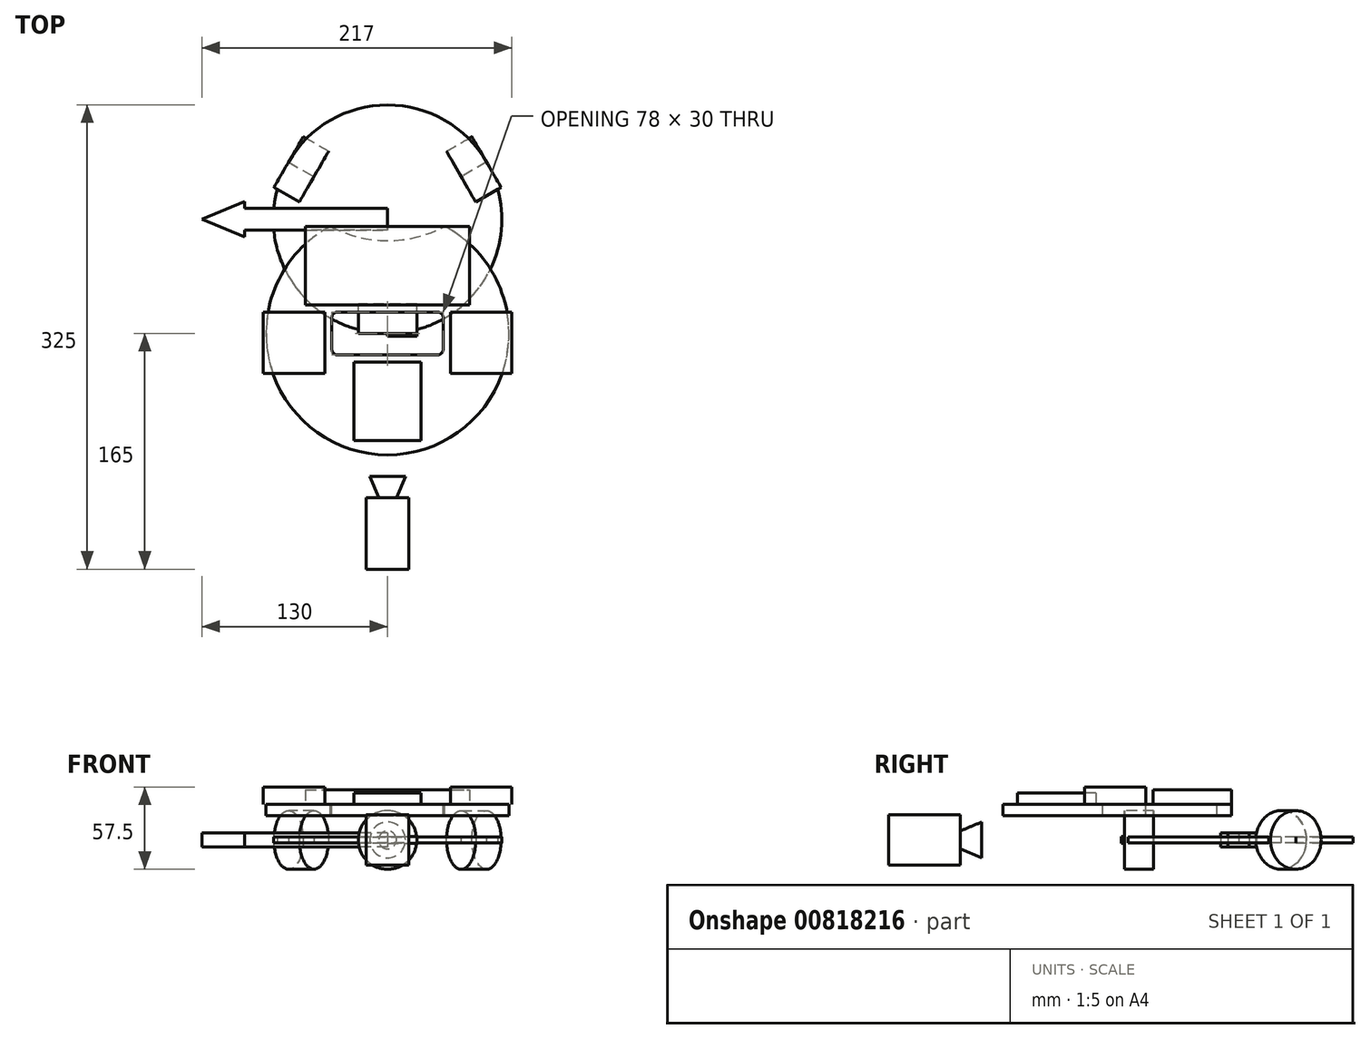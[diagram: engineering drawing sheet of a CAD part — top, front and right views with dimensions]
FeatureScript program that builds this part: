
annotation { "Feature Type Name" : "Feature", "Feature Type Description" : "" }
export const myFeature = defineFeature(function(context is Context, id is Id, definition is map)
    precondition{}
    {
        {
            var Q0;
            Q0=qCreatedBy(makeId("Top.planeOp"),FACE);
            var sketch = newSketch(context, id + "F0", { "sketchPlane" : qUnion([Q0])});
            skLineSegment(sketch, "E0.bottom", {"start": v(0, 0) * mm, "end": v(20.5, 0) * mm});
            skLineSegment(sketch, "E0.top", {"start": v(0, 20.5) * mm, "end": v(20.5, 20.5) * mm});
            skLineSegment(sketch, "E0.left", {"start": v(0, 0) * mm, "end": v(0, 20.5) * mm});
            skLineSegment(sketch, "E0.right", {"start": v(20.5, 0) * mm, "end": v(20.5, 20.5) * mm});
            skLineSegment(sketch, "E1", {"start": v(0, -100) * mm, "end": v(12.5, -100) * mm});
            skLineSegment(sketch, "E2", {"start": v(12.5, -100) * mm, "end": v(0, -130) * mm});
            skLineSegment(sketch, "E3.bottom", {"start": v(15, -115) * mm, "end": v(-15, -115) * mm});
            skLineSegment(sketch, "E3.top", {"start": v(15, -165) * mm, "end": v(-15, -165) * mm});
            skLineSegment(sketch, "E3.left", {"start": v(15, -115) * mm, "end": v(15, -165) * mm});
            skLineSegment(sketch, "E3.right", {"start": v(-15, -115) * mm, "end": v(-15, -165) * mm});
            skLineSegment(sketch, "E4", {"start": v(0, -100) * mm, "end": v(0, -130) * mm});
            skLineSegment(sketch, "E5.top", {"start": v(0, -2) * mm, "end": v(20.5, -2) * mm});
            skLineSegment(sketch, "E5.left", {"start": v(0, 0) * mm, "end": v(0, -2) * mm});
            skLineSegment(sketch, "E5.right", {"start": v(20.5, 0) * mm, "end": v(20.5, -2) * mm});
            skCircle(sketch, "E6", {"center": v(0, 80) * mm, "radius": 80 * mm});
            skLineSegment(sketch, "E7.bottom", {"start": v(0, 0) * mm, "end": v(-20.5, 0) * mm});
            skLineSegment(sketch, "E7.top", {"start": v(0, 20.5) * mm, "end": v(-20.5, 20.5) * mm});
            skLineSegment(sketch, "E7.right", {"start": v(-20.5, 0) * mm, "end": v(-20.5, 20.5) * mm});
            skLineSegment(sketch, "E8", {"start": v(-69.28, 40) * mm, "end": v(0, 80) * mm});
            skLineSegment(sketch, "E9", {"start": v(0, 80) * mm, "end": v(69.28, 40) * mm});
            skLineSegment(sketch, "E10", {"start": v(0, 0) * mm, "end": v(0, 80) * mm});
            skLineSegment(sketch, "E11.MirrorCS", {"start": v(79.53, 102.25) * mm, "end": v(61.78, 92) * mm});
            skLineSegment(sketch, "E12.MirrorCS", {"start": v(51.53, 109.75) * mm, "end": v(61.78, 92) * mm});
            skLineSegment(sketch, "E13.MirrorCS", {"start": v(69.28, 120) * mm, "end": v(51.53, 109.75) * mm});
            skLineSegment(sketch, "E14.MirrorCS", {"start": v(69.28, 120) * mm, "end": v(79.53, 102.25) * mm});
            skLineSegment(sketch, "E15.MirrorCS", {"start": v(-51.53, 109.75) * mm, "end": v(-61.78, 92) * mm});
            skLineSegment(sketch, "E16.MirrorCS", {"start": v(-79.53, 102.25) * mm, "end": v(-61.78, 92) * mm});
            skLineSegment(sketch, "E17.MirrorCS", {"start": v(-69.28, 120) * mm, "end": v(-79.53, 102.25) * mm});
            skLineSegment(sketch, "E18.MirrorCS", {"start": v(-69.28, 120) * mm, "end": v(-51.53, 109.75) * mm});
            skLineSegment(sketch, "E19.bottom", {"start": v(0, 72.5) * mm, "end": v(-100, 72.5) * mm});
            skLineSegment(sketch, "E19.top", {"start": v(0, 87.5) * mm, "end": v(-100, 87.5) * mm});
            skLineSegment(sketch, "E19.left", {"start": v(0, 72.5) * mm, "end": v(0, 87.5) * mm});
            skLineSegment(sketch, "E19.right", {"start": v(-100, 72.5) * mm, "end": v(-100, 87.5) * mm});
            skLineSegment(sketch, "E20", {"start": v(-130, 80) * mm, "end": v(-100, 67.5) * mm});
            skLineSegment(sketch, "E21", {"start": v(-130, 80) * mm, "end": v(0, 80) * mm});
            skLineSegment(sketch, "E22", {"start": v(-100, 72.5) * mm, "end": v(-100, 67.5) * mm});
            skLineSegment(sketch, "E23.MirrorCS", {"start": v(-130, 80) * mm, "end": v(-100, 92.5) * mm});
            skLineSegment(sketch, "E24.MirrorCS", {"start": v(-100, 87.5) * mm, "end": v(-100, 92.5) * mm});
            skSolve(sketch);
        }
        {
            var Q0;
            {var subQ0=sQuery(id+"F0.wireOp",EDGE,"E0.top");Q0=makeQuery(id+"F0.imprint","IMPRINT",FACE,{"disambiguationData":[TD([[makeQuery(id+"F0.imprint","IMPRINT",EDGE,{"derivedFrom":subQ0}),1.0]])]});}
            var Q1;
            {var subQ2=sQuery(id+"F0.wireOp",EDGE,"E7.top");Q1=makeQuery(id+"F0.imprint","IMPRINT",FACE,{"disambiguationData":[TD([[makeQuery(id+"F0.imprint","IMPRINT",EDGE,{"derivedFrom":subQ2}),-1.0]])]});}
            var Q2;
            {var subQ0=sQuery(id+"F0.wireOp",EDGE,"E8");Q2=makeQuery(id+"F0.imprint","IMPRINT",FACE,{"disambiguationData":[TD([[makeQuery(id+"F0.imprint","IMPRINT",EDGE,{"derivedFrom":subQ0}),1.0]])]});}
            var Q3;
            {var subQ11=sQuery(id+"F0.wireOp",EDGE,"E9");Q3=makeQuery(id+"F0.imprint","IMPRINT",FACE,{"disambiguationData":[TD([[makeQuery(id+"F0.imprint","IMPRINT",EDGE,{"derivedFrom":subQ11}),1.0]])]});}
            var Q4;
            {var subQ0=sQuery(id+"F0.wireOp",EDGE,"E19.bottom");var subQ1=sQuery(id+"F0.wireOp",EDGE,"E6");var subQ2=makeQuery(id+"F0.imprint","INTERSECT",VERTEX,{"derivedFrom":[subQ1,subQ0]});Q4=makeQuery(id+"F0.imprint","IMPRINT",FACE,{"disambiguationData":[TD([[makeQuery(id+"F0.imprint","IMPRINT",EDGE,{"disambiguationData":[TD([[subQ2,1.0]])],"derivedFrom":subQ1}),1.0]])]});}
            var Q5;
            {var subQ0=sQuery(id+"F0.wireOp",EDGE,"E19.top");var subQ1=sQuery(id+"F0.wireOp",EDGE,"E6");var subQ2=makeQuery(id+"F0.imprint","INTERSECT",VERTEX,{"derivedFrom":[subQ1,subQ0]});Q5=makeQuery(id+"F0.imprint","IMPRINT",FACE,{"disambiguationData":[TD([[makeQuery(id+"F0.imprint","IMPRINT",EDGE,{"disambiguationData":[TD([[subQ2,-1.0]])],"derivedFrom":subQ1}),1.0]])]});}
            var Q6;
            {var subQ1=sQuery(id+"F0.wireOp",EDGE,"E8");var subQ3=sQuery(id+"F0.wireOp",EDGE,"E19.bottom");var subQ4=makeQuery(id+"F0.imprint","INTERSECT",VERTEX,{"derivedFrom":[subQ1,subQ3]});Q6=makeQuery(id+"F0.imprint","IMPRINT",FACE,{"disambiguationData":[TD([[makeQuery(id+"F0.imprint","IMPRINT",EDGE,{"disambiguationData":[TD([[subQ4,1.0]])],"derivedFrom":subQ3}),-1.0]])]});}
            extrude(context, id + "F1", {"entities" : qUnion([Q0, Q1, Q2, Q3, Q4, Q5, Q6]), "endBound" : BoundingType.SYMMETRIC, "depth" : 4 * mm, "offsetDistance" : 25 * mm});
        }
        {
            var Q0;
            {var subQ0=sQuery(id+"F0.wireOp",EDGE,"E0.top");Q0=makeQuery(id+"F0.imprint","IMPRINT",FACE,{"disambiguationData":[TD([[makeQuery(id+"F0.imprint","IMPRINT",EDGE,{"derivedFrom":subQ0}),-1.0]])]});}
            var Q1;
            {var subQ0=sQuery(id+"F0.wireOp",EDGE,"E0.bottom");Q1=makeQuery(id+"F0.imprint","IMPRINT",FACE,{"disambiguationData":[TD([[makeQuery(id+"F0.imprint","IMPRINT",EDGE,{"derivedFrom":subQ0}),1.0]])]});}
            var Q2;
            Q2=sQuery(id+"F0.wireOp",EDGE,"E0.left");
            revolve(context, id + "F2", {"surfaceOperationType" : NewSurfaceOperationType.NEW, "entities" : qUnion([Q0, Q1]), "axis" : qUnion([Q2]), "revolveType" : RevolveType.FULL});
        }
        {
            var Q0;
            {var subQ0=sQuery(id+"F0.wireOp",EDGE,"E1");Q0=makeQuery(id+"F0.imprint","IMPRINT",FACE,{"disambiguationData":[TD([[makeQuery(id+"F0.imprint","IMPRINT",EDGE,{"derivedFrom":subQ0}),-1.0]])]});}
            var Q1;
            Q1=sQuery(id+"F0.wireOp",EDGE,"E4");
            revolve(context, id + "F3", {"surfaceOperationType" : NewSurfaceOperationType.NEW, "entities" : qUnion([Q0]), "axis" : qUnion([Q1]), "revolveType" : RevolveType.FULL});
        }
        {
            var Q0;
            Q0=makeQuery(id+"F0.imprint","IMPRINT",FACE,{"disambiguationData":[TD([[makeQuery(id+"F0.imprint","IMPRINT",EDGE,{"derivedFrom":sQuery(id+"F0.wireOp",EDGE,"E3.top")}),-1.0]])]});
            var Q1;
            {var subQ0=sQuery(id+"F0.wireOp",EDGE,"E4");var subQ1=sQuery(id+"F0.wireOp",EDGE,"E2");var subQ2=makeQuery(id+"F0.imprint","INTERSECT",VERTEX,{"derivedFrom":[subQ1,subQ0]});Q1=makeQuery(id+"F0.imprint","IMPRINT",FACE,{"disambiguationData":[TD([[makeQuery(id+"F0.imprint","IMPRINT",EDGE,{"disambiguationData":[TD([[subQ2,1.0]])],"derivedFrom":subQ1}),-1.0]])]});}
            extrude(context, id + "F4", {"entities" : qUnion([Q0, Q1]), "operationType" : NewBodyOperationType.ADD, "endBound" : BoundingType.SYMMETRIC, "depth" : 35 * mm, "offsetDistance" : 25 * mm});
        }
        {
            var Q0;
            Q0=makeQuery(id+"F0.imprint","IMPRINT",FACE,{"disambiguationData":[TD([[makeQuery(id+"F0.imprint","IMPRINT",EDGE,{"derivedFrom":sQuery(id+"F0.wireOp",EDGE,"E0.bottom")}),-1.0]])]});
            extrude(context, id + "F5", {"entities" : qUnion([Q0]), "endBound" : BoundingType.SYMMETRIC, "depth" : 5 * mm, "offsetDistance" : 25 * mm});
        }
        {
            var Q0;
            {var subQ4=sQuery(id+"F0.wireOp",EDGE,"E12.MirrorCS");Q0=makeQuery(id+"F0.imprint","IMPRINT",FACE,{"disambiguationData":[TD([[makeQuery(id+"F0.imprint","IMPRINT",EDGE,{"derivedFrom":subQ4}),1.0]])]});}
            var Q1;
            {var subQ0=sQuery(id+"F0.wireOp",EDGE,"E14.MirrorCS");Q1=makeQuery(id+"F0.imprint","IMPRINT",FACE,{"disambiguationData":[TD([[makeQuery(id+"F0.imprint","IMPRINT",EDGE,{"derivedFrom":subQ0}),-1.0]])]});}
            var Q2;
            Q2=sQuery(id+"F0.wireOp",EDGE,"E13.MirrorCS");
            revolve(context, id + "F6", {"surfaceOperationType" : NewSurfaceOperationType.NEW, "entities" : qUnion([Q0, Q1]), "axis" : qUnion([Q2]), "revolveType" : RevolveType.FULL});
        }
        {
            var Q0;
            {var subQ4=sQuery(id+"F0.wireOp",EDGE,"E15.MirrorCS");Q0=makeQuery(id+"F0.imprint","IMPRINT",FACE,{"disambiguationData":[TD([[makeQuery(id+"F0.imprint","IMPRINT",EDGE,{"derivedFrom":subQ4}),-1.0]])]});}
            var Q1;
            {var subQ0=sQuery(id+"F0.wireOp",EDGE,"E17.MirrorCS");Q1=makeQuery(id+"F0.imprint","IMPRINT",FACE,{"disambiguationData":[TD([[makeQuery(id+"F0.imprint","IMPRINT",EDGE,{"derivedFrom":subQ0}),1.0]])]});}
            var Q2;
            Q2=sQuery(id+"F0.wireOp",EDGE,"E18.MirrorCS");
            revolve(context, id + "F7", {"surfaceOperationType" : NewSurfaceOperationType.NEW, "entities" : qUnion([Q0, Q1]), "axis" : qUnion([Q2]), "revolveType" : RevolveType.FULL});
        }
        {
            var Q0;
            {var subQ4=sQuery(id+"F0.wireOp",EDGE,"E20");Q0=makeQuery(id+"F0.imprint","IMPRINT",FACE,{"disambiguationData":[TD([[makeQuery(id+"F0.imprint","IMPRINT",EDGE,{"derivedFrom":subQ4}),1.0]])]});}
            var Q1;
            {var subQ4=sQuery(id+"F0.wireOp",EDGE,"E23.MirrorCS");Q1=makeQuery(id+"F0.imprint","IMPRINT",FACE,{"disambiguationData":[TD([[makeQuery(id+"F0.imprint","IMPRINT",EDGE,{"derivedFrom":subQ4}),-1.0]])]});}
            var Q2;
            {var subQ0=sQuery(id+"F0.wireOp",EDGE,"E19.top");var subQ1=sQuery(id+"F0.wireOp",EDGE,"E6");var subQ2=makeQuery(id+"F0.imprint","INTERSECT",VERTEX,{"derivedFrom":[subQ1,subQ0]});Q2=makeQuery(id+"F0.imprint","IMPRINT",FACE,{"disambiguationData":[TD([[makeQuery(id+"F0.imprint","IMPRINT",EDGE,{"disambiguationData":[TD([[subQ2,-1.0]])],"derivedFrom":subQ1}),-1.0]])]});}
            var Q3;
            {var subQ0=sQuery(id+"F0.wireOp",EDGE,"E19.bottom");var subQ1=sQuery(id+"F0.wireOp",EDGE,"E6");var subQ2=makeQuery(id+"F0.imprint","INTERSECT",VERTEX,{"derivedFrom":[subQ1,subQ0]});Q3=makeQuery(id+"F0.imprint","IMPRINT",FACE,{"disambiguationData":[TD([[makeQuery(id+"F0.imprint","IMPRINT",EDGE,{"disambiguationData":[TD([[subQ2,1.0]])],"derivedFrom":subQ1}),-1.0]])]});}
            var Q4;
            {var subQ0=sQuery(id+"F0.wireOp",EDGE,"E19.top");var subQ1=sQuery(id+"F0.wireOp",EDGE,"E6");var subQ2=makeQuery(id+"F0.imprint","INTERSECT",VERTEX,{"derivedFrom":[subQ1,subQ0]});Q4=makeQuery(id+"F0.imprint","IMPRINT",FACE,{"disambiguationData":[TD([[makeQuery(id+"F0.imprint","IMPRINT",EDGE,{"disambiguationData":[TD([[subQ2,-1.0]])],"derivedFrom":subQ1}),1.0]])]});}
            var Q5;
            {var subQ0=sQuery(id+"F0.wireOp",EDGE,"E19.bottom");var subQ1=sQuery(id+"F0.wireOp",EDGE,"E6");var subQ2=makeQuery(id+"F0.imprint","INTERSECT",VERTEX,{"derivedFrom":[subQ1,subQ0]});Q5=makeQuery(id+"F0.imprint","IMPRINT",FACE,{"disambiguationData":[TD([[makeQuery(id+"F0.imprint","IMPRINT",EDGE,{"disambiguationData":[TD([[subQ2,1.0]])],"derivedFrom":subQ1}),1.0]])]});}
            var Q6;
            {var subQ1=sQuery(id+"F0.wireOp",EDGE,"E8");var subQ3=sQuery(id+"F0.wireOp",EDGE,"E19.bottom");var subQ4=makeQuery(id+"F0.imprint","INTERSECT",VERTEX,{"derivedFrom":[subQ1,subQ3]});Q6=makeQuery(id+"F0.imprint","IMPRINT",FACE,{"disambiguationData":[TD([[makeQuery(id+"F0.imprint","IMPRINT",EDGE,{"disambiguationData":[TD([[subQ4,1.0]])],"derivedFrom":subQ3}),-1.0]])]});}
            extrude(context, id + "F8", {"entities" : qUnion([Q0, Q1, Q2, Q3, Q4, Q5, Q6]), "operationType" : NewBodyOperationType.ADD, "endBound" : BoundingType.SYMMETRIC, "depth" : 10 * mm, "offsetDistance" : 25 * mm});
        }
        {
            var Q0;
            Q0=qCreatedBy(makeId("Top.planeOp"),FACE);
            cPlane(context, id + "F9", {"entities" : qUnion([Q0]), "cplaneType" : CPlaneType.OFFSET, "offset" : 25 * mm, "width" : 150 * mm, "height" : 150 * mm});
        }
        {
            var Q0;
            Q0=qCreatedBy(id+"F9.planeOp",FACE);
            var sketch = newSketch(context, id + "F10", { "sketchPlane" : qUnion([Q0])});
            skPoint(sketch, "E25.0", {"position": v(0, 0) * mm});
            skArc(sketch, "E26", {"start": v(-40, 75) * mm, "mid": v(0, -85) * mm, "end": v(40, 75) * mm});
            skLineSegment(sketch, "E27", {"start": v(0, 0) * mm, "end": v(0, 85) * mm, "construction": true});
            skPoint(sketch, "E28", {"position": v(0, 65) * mm});
            skLineSegment(sketch, "E29", {"start": v(0, 65) * mm, "end": v(0, 85) * mm});
            skPoint(sketch, "E30", {"position": v(0, 75) * mm});
            skLineSegment(sketch, "E31", {"start": v(40, 75) * mm, "end": v(-40, 75) * mm, "construction": true});
            skArc(sketch, "E32", {"start": v(-40, 75) * mm, "mid": v(0, 65) * mm, "end": v(40, 75) * mm});
            skCircle(sketch, "E33", {"center": v(-35, 11) * mm, "radius": 4 * mm});
            skLineSegment(sketch, "E34", {"start": v(-35, 15) * mm, "end": v(0, 15) * mm});
            skLineSegment(sketch, "E35", {"start": v(0, 0) * mm, "end": v(-85, 0) * mm, "construction": true});
            skLineSegment(sketch, "E36", {"start": v(-39, 11) * mm, "end": v(-39, 0) * mm});
            skCircle(sketch, "E37.MirrorC", {"center": v(35, 11) * mm, "radius": 4 * mm});
            skLineSegment(sketch, "E38.MirrorCS", {"start": v(39, 11) * mm, "end": v(39, 0) * mm});
            skLineSegment(sketch, "E39.MirrorCS", {"start": v(35, 15) * mm, "end": v(0, 15) * mm});
            skCircle(sketch, "E40.MirrorC", {"center": v(-35, -11) * mm, "radius": 4 * mm});
            skCircle(sketch, "E41.MirrorC", {"center": v(35, -11) * mm, "radius": 4 * mm});
            skLineSegment(sketch, "E42.MirrorCS", {"start": v(-39, -11) * mm, "end": v(-39, 0) * mm});
            skLineSegment(sketch, "E43.MirrorCS", {"start": v(39, -11) * mm, "end": v(39, 0) * mm});
            skLineSegment(sketch, "E44.MirrorCS", {"start": v(35, -15) * mm, "end": v(0, -15) * mm});
            skLineSegment(sketch, "E45.MirrorCS", {"start": v(-35, -15) * mm, "end": v(0, -15) * mm});
            skLineSegment(sketch, "E46.bottom", {"start": v(-57.5, 75) * mm, "end": v(57.5, 75) * mm});
            skLineSegment(sketch, "E46.top", {"start": v(-57.5, 20) * mm, "end": v(57.5, 20) * mm});
            skLineSegment(sketch, "E46.left", {"start": v(-57.5, 75) * mm, "end": v(-57.5, 20) * mm});
            skLineSegment(sketch, "E46.right", {"start": v(57.5, 75) * mm, "end": v(57.5, 20) * mm});
            skPoint(sketch, "E47", {"position": v(0, 20) * mm});
            skLineSegment(sketch, "E48.bottom", {"start": v(-23.5, -20) * mm, "end": v(23.5, -20) * mm});
            skLineSegment(sketch, "E48.top", {"start": v(-23.5, -75) * mm, "end": v(23.5, -75) * mm});
            skLineSegment(sketch, "E48.left", {"start": v(-23.5, -20) * mm, "end": v(-23.5, -75) * mm});
            skLineSegment(sketch, "E48.right", {"start": v(23.5, -20) * mm, "end": v(23.5, -75) * mm});
            skPoint(sketch, "E49", {"position": v(0, -20) * mm});
            skLineSegment(sketch, "E50.bottom", {"start": v(44, 15) * mm, "end": v(87, 15) * mm});
            skLineSegment(sketch, "E50.top", {"start": v(44, -28) * mm, "end": v(87, -28) * mm});
            skLineSegment(sketch, "E50.left", {"start": v(44, 15) * mm, "end": v(44, -28) * mm});
            skLineSegment(sketch, "E50.right", {"start": v(87, 15) * mm, "end": v(87, -28) * mm});
            skLineSegment(sketch, "E51.MirrorCS", {"start": v(-44, 15) * mm, "end": v(-44, -28) * mm});
            skLineSegment(sketch, "E52.MirrorCS", {"start": v(-44, 15) * mm, "end": v(-87, 15) * mm});
            skLineSegment(sketch, "E53.MirrorCS", {"start": v(-87, 15) * mm, "end": v(-87, -28) * mm});
            skLineSegment(sketch, "E54.MirrorCS", {"start": v(-44, -28) * mm, "end": v(-87, -28) * mm});
            skSolve(sketch);
        }
        {
            var Q0;
            {var subQ15=sQuery(id+"F10.wireOp",EDGE,"E34");Q0=makeQuery(id+"F10.imprint","IMPRINT",FACE,{"disambiguationData":[TD([[makeQuery(id+"F10.imprint","IMPRINT",EDGE,{"derivedFrom":subQ15}),1.0]])]});}
            var Q1;
            {var subQ5=sQuery(id+"F10.wireOp",EDGE,"E51.MirrorCS");Q1=makeQuery(id+"F10.imprint","IMPRINT",FACE,{"disambiguationData":[TD([[makeQuery(id+"F10.imprint","IMPRINT",EDGE,{"derivedFrom":subQ5}),-1.0]])]});}
            var Q2;
            Q2=makeQuery(id+"F10.imprint","IMPRINT",FACE,{"disambiguationData":[TD([[makeQuery(id+"F10.imprint","IMPRINT",EDGE,{"derivedFrom":sQuery(id+"F10.wireOp",EDGE,"E48.bottom")}),-1.0]])]});
            var Q3;
            {var subQ5=sQuery(id+"F10.wireOp",EDGE,"E50.left");Q3=makeQuery(id+"F10.imprint","IMPRINT",FACE,{"disambiguationData":[TD([[makeQuery(id+"F10.imprint","IMPRINT",EDGE,{"derivedFrom":subQ5}),1.0]])]});}
            var Q4;
            {var subQ8=sQuery(id+"F10.wireOp",EDGE,"E46.top");Q4=makeQuery(id+"F10.imprint","IMPRINT",FACE,{"disambiguationData":[TD([[makeQuery(id+"F10.imprint","IMPRINT",EDGE,{"derivedFrom":subQ8}),1.0]])]});}
            extrude(context, id + "F11", {"entities" : qUnion([Q0, Q1, Q2, Q3, Q4]), "oppositeDirection" : true, "depth" : 8 * mm, "offsetDistance" : 25 * mm});
        }
        {
            var Q0;
            {var subQ0=sQuery(id+"F10.wireOp",EDGE,"E46.bottom");var subQ1=sQuery(id+"F10.wireOp",EDGE,"E29");var subQ2=makeQuery(id+"F10.imprint","INTERSECT",VERTEX,{"derivedFrom":[subQ1,subQ0]});Q0=makeQuery(id+"F10.imprint","IMPRINT",FACE,{"disambiguationData":[TD([[makeQuery(id+"F10.imprint","IMPRINT",EDGE,{"disambiguationData":[TD([[subQ2,1.0]])],"derivedFrom":subQ1}),-1.0]])]});}
            var Q1;
            {var subQ0=sQuery(id+"F10.wireOp",EDGE,"E46.bottom");var subQ1=sQuery(id+"F10.wireOp",EDGE,"E29");var subQ2=makeQuery(id+"F10.imprint","INTERSECT",VERTEX,{"derivedFrom":[subQ1,subQ0]});Q1=makeQuery(id+"F10.imprint","IMPRINT",FACE,{"disambiguationData":[TD([[makeQuery(id+"F10.imprint","IMPRINT",EDGE,{"disambiguationData":[TD([[subQ2,1.0]])],"derivedFrom":subQ1}),1.0]])]});}
            var Q2;
            {var subQ1=sQuery(id+"F10.wireOp",EDGE,"E26");var subQ3=sQuery(id+"F10.wireOp",EDGE,"E46.left");var subQ4=makeQuery(id+"F10.imprint","INTERSECT",VERTEX,{"derivedFrom":[subQ1,subQ3]});Q2=makeQuery(id+"F10.imprint","IMPRINT",FACE,{"disambiguationData":[TD([[makeQuery(id+"F10.imprint","IMPRINT",EDGE,{"disambiguationData":[TD([[subQ4,1.0]])],"derivedFrom":subQ3}),1.0]])]});}
            var Q3;
            {var subQ1=sQuery(id+"F10.wireOp",EDGE,"E26");var subQ3=sQuery(id+"F10.wireOp",EDGE,"E46.right");var subQ4=makeQuery(id+"F10.imprint","INTERSECT",VERTEX,{"derivedFrom":[subQ1,subQ3]});Q3=makeQuery(id+"F10.imprint","IMPRINT",FACE,{"disambiguationData":[TD([[makeQuery(id+"F10.imprint","IMPRINT",EDGE,{"disambiguationData":[TD([[subQ4,1.0]])],"derivedFrom":subQ3}),-1.0]])]});}
            var Q4;
            {var subQ8=sQuery(id+"F10.wireOp",EDGE,"E46.top");Q4=makeQuery(id+"F10.imprint","IMPRINT",FACE,{"disambiguationData":[TD([[makeQuery(id+"F10.imprint","IMPRINT",EDGE,{"derivedFrom":subQ8}),1.0]])]});}
            extrude(context, id + "F12", {"entities" : qUnion([Q0, Q1, Q2, Q3, Q4]), "depth" : 10 * mm, "offsetDistance" : 25 * mm});
        }
        {
            var Q0;
            {var subQ5=sQuery(id+"F10.wireOp",EDGE,"E53.MirrorCS");Q0=makeQuery(id+"F10.imprint","IMPRINT",FACE,{"disambiguationData":[TD([[makeQuery(id+"F10.imprint","IMPRINT",EDGE,{"derivedFrom":subQ5}),1.0]])]});}
            var Q1;
            {var subQ5=sQuery(id+"F10.wireOp",EDGE,"E51.MirrorCS");Q1=makeQuery(id+"F10.imprint","IMPRINT",FACE,{"disambiguationData":[TD([[makeQuery(id+"F10.imprint","IMPRINT",EDGE,{"derivedFrom":subQ5}),-1.0]])]});}
            var Q2;
            {var subQ5=sQuery(id+"F10.wireOp",EDGE,"E50.left");Q2=makeQuery(id+"F10.imprint","IMPRINT",FACE,{"disambiguationData":[TD([[makeQuery(id+"F10.imprint","IMPRINT",EDGE,{"derivedFrom":subQ5}),1.0]])]});}
            var Q3;
            {var subQ5=sQuery(id+"F10.wireOp",EDGE,"E50.right");Q3=makeQuery(id+"F10.imprint","IMPRINT",FACE,{"disambiguationData":[TD([[makeQuery(id+"F10.imprint","IMPRINT",EDGE,{"derivedFrom":subQ5}),-1.0]])]});}
            extrude(context, id + "F13", {"entities" : qUnion([Q0, Q1, Q2, Q3]), "depth" : 12 * mm, "offsetDistance" : 25 * mm});
        }
        {
            var Q0;
            Q0=makeQuery(id+"F10.imprint","IMPRINT",FACE,{"disambiguationData":[TD([[makeQuery(id+"F10.imprint","IMPRINT",EDGE,{"derivedFrom":sQuery(id+"F10.wireOp",EDGE,"E48.bottom")}),-1.0]])]});
            extrude(context, id + "F14", {"entities" : qUnion([Q0]), "operationType" : NewBodyOperationType.ADD, "depth" : 8 * mm, "offsetDistance" : 25 * mm});
        }
    });
